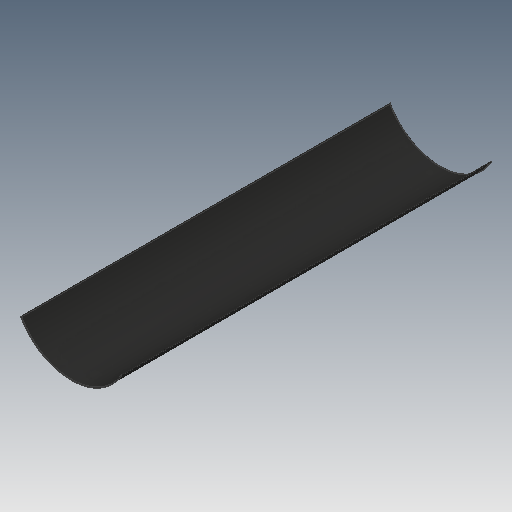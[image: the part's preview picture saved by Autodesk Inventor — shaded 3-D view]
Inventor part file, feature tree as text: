
AUTODESK INVENTOR PART (.ipt)
format: ipt  version: 2023.5 (Build 275446000, 446)  size: 208,384 bytes
history: native  units: in
note: dims shown in document units (in); Inventor stores cm internally (conversion verified against a paired STEP export)
features: sweep x1
ambient origin geometry x8: Origin, YZ Plane, XZ Plane, XY Plane, X Axis, Y Axis, Z Axis, Center Point
bodies: Solid1 (feature_tree)
feature tree (1):
  sweep  "Sweep1"
